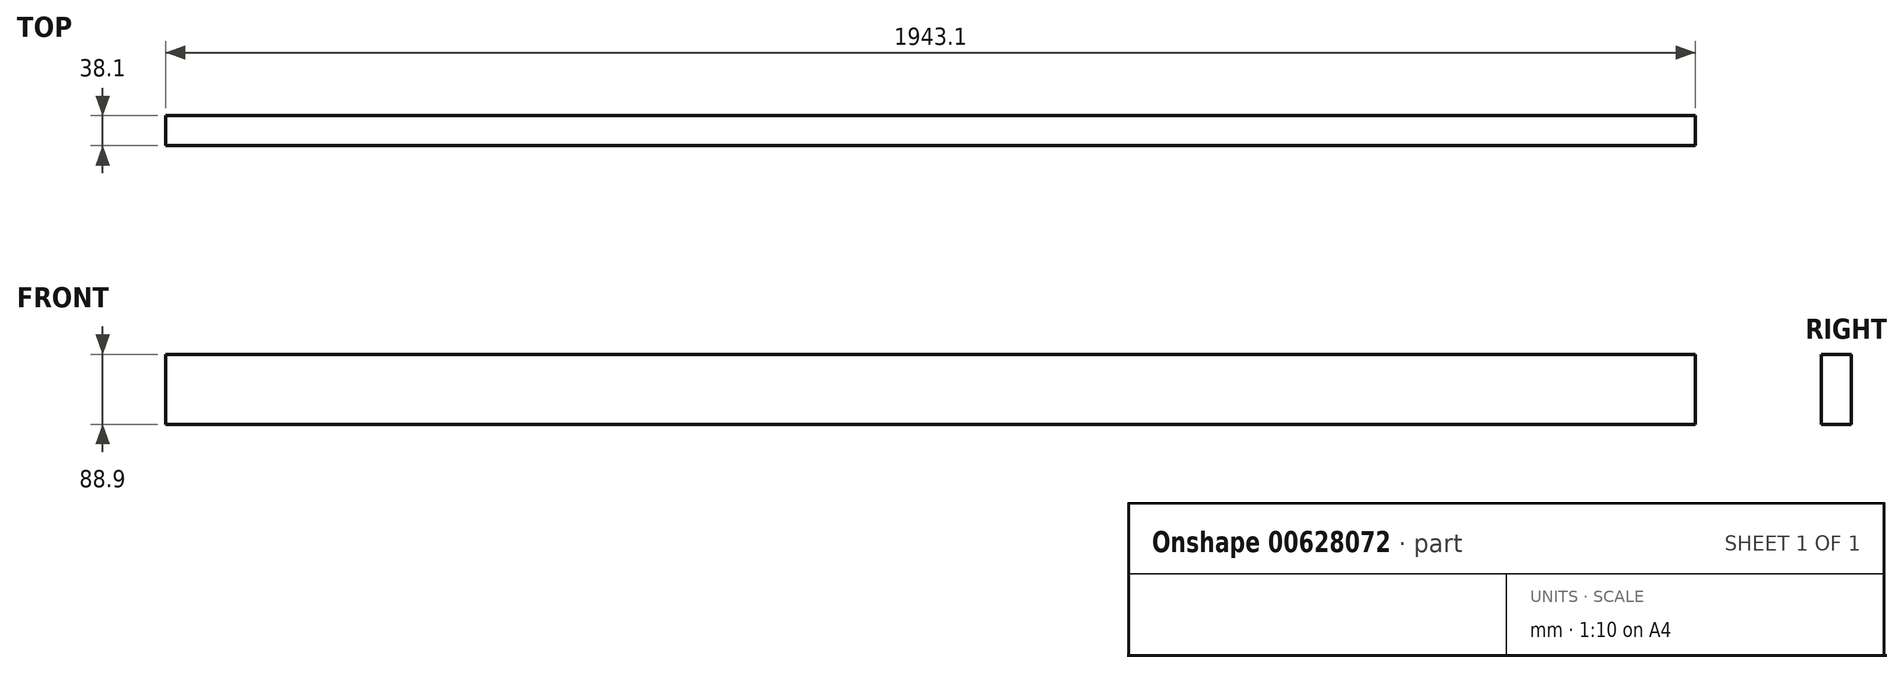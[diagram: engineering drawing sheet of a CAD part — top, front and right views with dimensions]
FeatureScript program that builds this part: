
annotation { "Feature Type Name" : "Feature", "Feature Type Description" : "" }
export const myFeature = defineFeature(function(context is Context, id is Id, definition is map)
    precondition{}
    {
        {
            var Q0;
            Q0=qCreatedBy(makeId("Front.planeOp"),FACE);
            var sketch = newSketch(context, id + "F0", { "sketchPlane" : qUnion([Q0])});
            skLineSegment(sketch, "E0.bottom", {"start": v(-1221.46, 70.64) * mm, "end": v(721.64, 70.64) * mm});
            skLineSegment(sketch, "E0.top", {"start": v(-1221.46, -18.26) * mm, "end": v(721.64, -18.26) * mm});
            skLineSegment(sketch, "E0.left", {"start": v(-1221.46, 70.64) * mm, "end": v(-1221.46, -18.26) * mm});
            skLineSegment(sketch, "E0.right", {"start": v(721.64, 70.64) * mm, "end": v(721.64, -18.26) * mm});
            skSolve(sketch);
        }
        {
            var Q0;
            Q0 = qSketchRegion(id + "F0", true);
            extrude(context, id + "F1", {"entities" : qUnion([Q0]), "depth" : 38.1 * mm, "offsetDistance" : 25.4 * mm});
        }
    });
